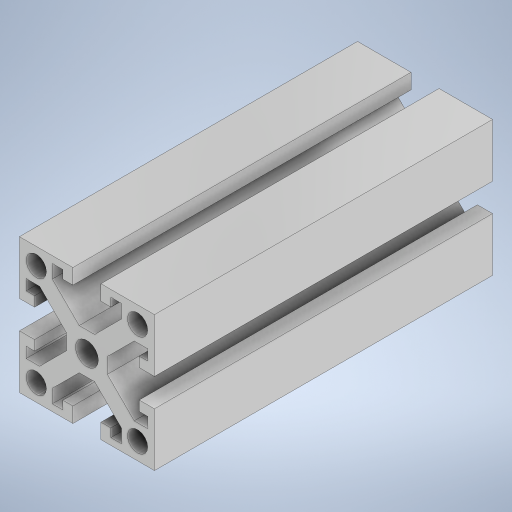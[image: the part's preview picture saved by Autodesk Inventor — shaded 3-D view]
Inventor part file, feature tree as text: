
AUTODESK INVENTOR PART (.ipt)
format: ipt  version: 2024.1 (Build 281209000, 209)  size: 315,904 bytes
history: native  units: in
note: dims shown in document units (in); Inventor stores cm internally (conversion verified against a paired STEP export)
features: extrude x1, plane x1, sketch x1
ambient origin geometry x8: Origin, YZ Plane, XZ Plane, XY Plane, X Axis, Y Axis, Z Axis, Center Point
bodies: Solid1 (feature_tree)
feature tree (3):
  extrude  "Extrusion1"  TaperAngle=45.0deg  [1 undecoded]
  plane  "Work Plane1"
  sketch  "Sketch1"  dims[d0=0.2677in d1=45.0deg d2=0.7874in d3=0.2362in d4=0.5906in d5=0.4035in d6=0.2795in d7=0.1634in d8=0.1772in d9=0.0787in d10=0.5492in d11=0.2362in d12=1.5748in d14=360.0deg d16=3.9425in d17=0.0in d18=0.0197in d19=0.0344in d20=0.0197in d21=0.0344in]
note: 1 required parameter value undecoded (feature->parameter linkage not recoverable at this tier; creation-order binding heuristic only, values carry confidence <= 0.55)
